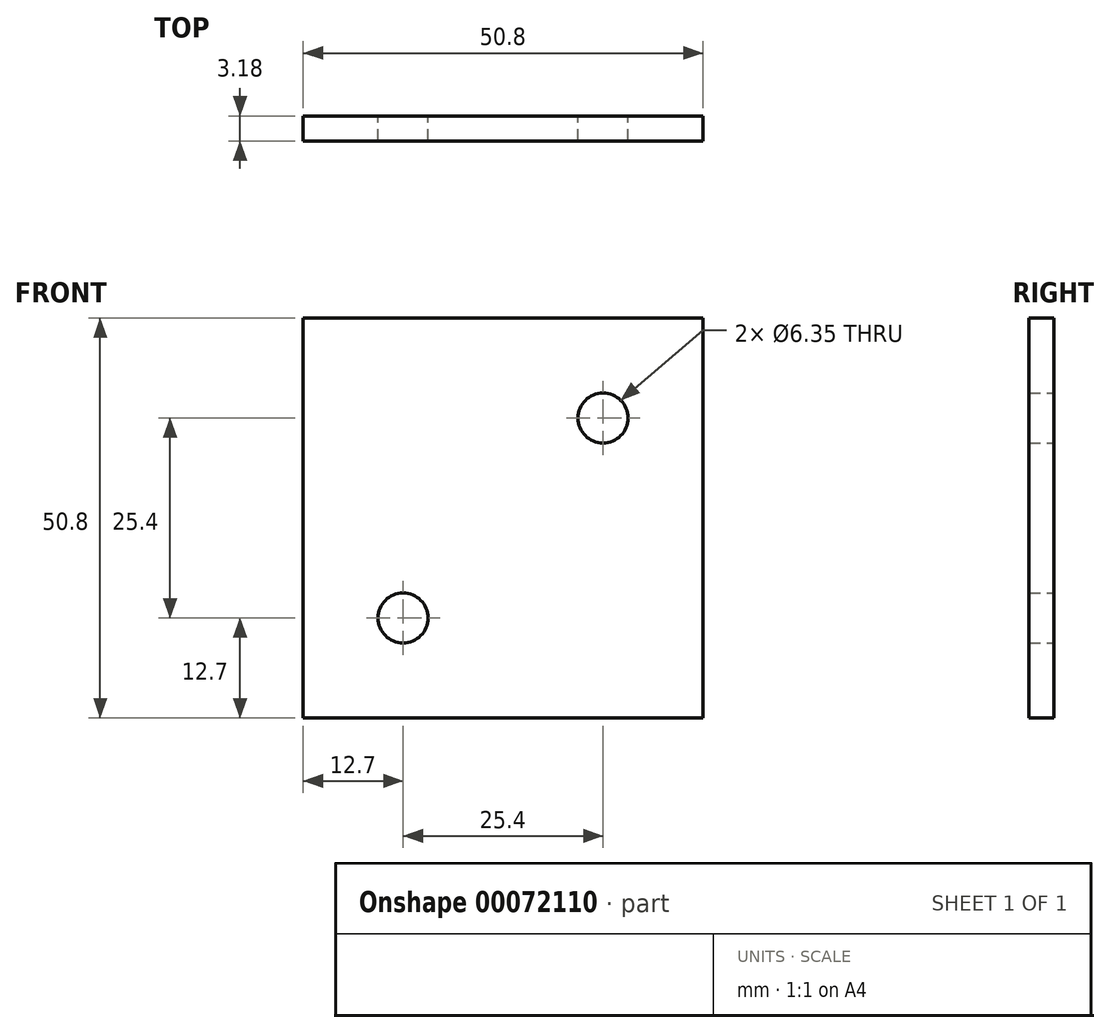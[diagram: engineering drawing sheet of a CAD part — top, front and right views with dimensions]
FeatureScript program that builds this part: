
annotation { "Feature Type Name" : "Feature", "Feature Type Description" : "" }
export const myFeature = defineFeature(function(context is Context, id is Id, definition is map)
    precondition{}
    {
        {
            var Q0;
            Q0=qCreatedBy(makeId("Front.planeOp"),FACE);
            var sketch = newSketch(context, id + "F0", { "sketchPlane" : qUnion([Q0])});
            skLineSegment(sketch, "E0.bottom", {"start": v(0, 0) * mm, "end": v(50.8, 0) * mm});
            skLineSegment(sketch, "E0.top", {"start": v(0, 50.8) * mm, "end": v(50.8, 50.8) * mm});
            skLineSegment(sketch, "E0.left", {"start": v(0, 0) * mm, "end": v(0, 50.8) * mm});
            skLineSegment(sketch, "E0.right", {"start": v(50.8, 0) * mm, "end": v(50.8, 50.8) * mm});
            skCircle(sketch, "E1", {"center": v(12.7, 12.7) * mm, "radius": 3.18 * mm});
            skCircle(sketch, "E2", {"center": v(38.1, 38.1) * mm, "radius": 3.18 * mm});
            skSolve(sketch);
        }
        {
            var Q0;
            Q0=makeQuery(id+"F0.imprint","IMPRINT",FACE,{"disambiguationData":[TD([[makeQuery(id+"F0.imprint","IMPRINT",EDGE,{"derivedFrom":sQuery(id+"F0.wireOp",EDGE,"E0.bottom")}),1.0]])]});
            extrude(context, id + "F1", {"entities" : qUnion([Q0]), "depth" : 3.17 * mm});
        }
    });
